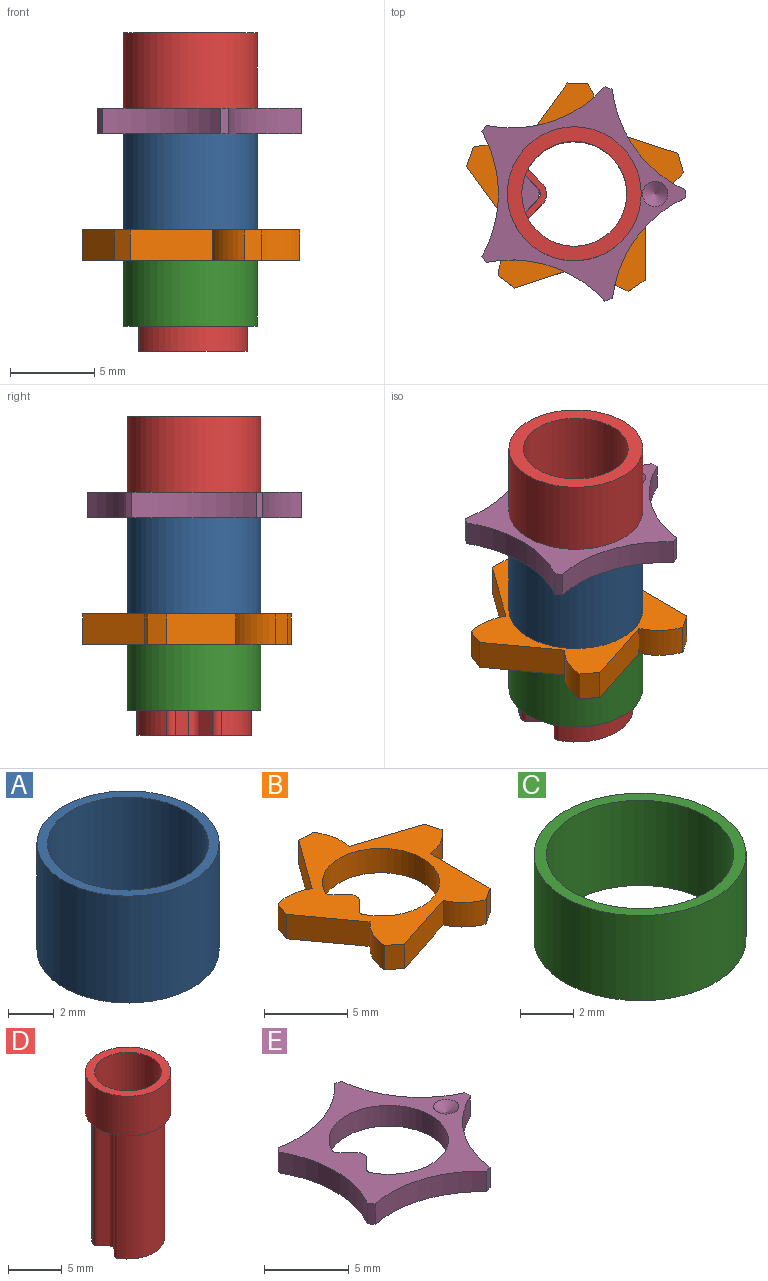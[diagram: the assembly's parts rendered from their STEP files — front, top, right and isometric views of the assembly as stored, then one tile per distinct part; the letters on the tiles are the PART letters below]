
ASSEMBLY  parts=5 mates=4
PART A: 4 faces, bbox 7.9x7.9x5.7 mm
  f0: cylinder r=3.51mm len=7.02mm, axis (0,0,-1), area 125.7mm2, adj f2,f3
  f1: cylinder r=3.97mm len=7.94mm, axis (0,0,-1), area 142.2mm2, adj f2,f3
  f2: plane 7.94x7.94mm, normal (0,0,1), area 10.8mm2, adj f0,f1
  f3: plane 7.94x7.94mm, normal (0,0,-1), area 10.8mm2, adj f0,f1
PART B: 23 faces, bbox 12.9x12.4x1.8 mm
  f0: plane 5.09x1.8mm, normal (1,0,0), area 9.2mm2, adj f1,f20,f21,f22
  f1: cylinder r=3.29mm len=2.28mm, axis (0,0,-1), area 4.8mm2, adj f0,f2,f21,f22
  f2: plane 1.8x1.15mm, normal (0.96,0.28,0), area 2.2mm2, adj f1,f3,f21,f22
  f3: plane 4.84x1.8mm, normal (0.31,0.95,0), area 9.2mm2, adj f2,f4,f21,f22
  f4: cylinder r=3.29mm len=2.56mm, axis (0,0,-1), area 4.8mm2, adj f3,f5,f21,f22
  f5: plane 1.8x1.2mm, normal (0.03,1,0), area 2.2mm2, adj f4,f6,f21,f22
  f6: plane 4.12x2.99mm, normal (-0.81,0.59,0), area 9.2mm2, adj f5,f7,f21,f22
  f7: cylinder r=3.29mm len=2.59mm, axis (0,0,-1), area 4.8mm2, adj f6,f8,f21,f22
  f8: plane 1.8x1.13mm, normal (-0.94,0.34,0), area 2.2mm2, adj f7,f9,f21,f22
  f9: plane 4.12x2.99mm, normal (-0.81,-0.59,0), area 9.2mm2, adj f8,f10,f21,f22
  f10: cylinder r=3.29mm len=2.37mm, axis (0,0,-1), area 4.8mm2, adj f9,f11,f21,f22
  f11: plane 1.8x0.95mm, normal (-0.61,-0.79,0), area 2.2mm2, adj f10,f12,f21,f22
  f12: plane 4.84x1.8mm, normal (0.31,-0.95,0), area 9.2mm2, adj f11,f13,f21,f22
  f13: cylinder r=3.29mm len=1.91mm, axis (0,0,-1), area 4.8mm2, adj f12,f20,f21,f22
  f14: cylinder r=3.53mm len=7.06mm, axis (0,0,-1), area 33.9mm2, adj f15,f19,f21,f22
  f15: cylinder r=0.3mm len=1.8mm, axis (0,0,-1), area 0.7mm2, adj f14,f16,f21,f22
  f16: plane 1.8x0.83mm, normal (0.71,-0.71,0), area 2.1mm2, adj f15,f17,f21,f22
  f17: cylinder r=0.6mm len=1.8mm, axis (0,0,-1), area 1.7mm2, adj f16,f18,f21,f22
  f18: plane 1.8x0.83mm, normal (0.71,0.71,0), area 2.1mm2, adj f17,f19,f21,f22
  f19: cylinder r=0.3mm len=1.8mm, axis (0,0,-1), area 0.7mm2, adj f14,f18,f21,f22
  f20: plane 1.8x0.99mm, normal (0.56,-0.83,0), area 2.2mm2, adj f0,f13,f21,f22
  f21: plane 12.87x12.36mm, normal (0,0,1), area 52.2mm2, adj f0,f1,f2,f3,f4,f5,f6,f7
  f22: plane 12.87x12.36mm, normal (0,0,-1), area 52.2mm2, adj f0,f1,f2,f3,f4,f5,f6,f7
PART C: 4 faces, bbox 7.9x7.9x3.9 mm
  f0: cylinder r=3.51mm len=7.02mm, axis (0,0,-1), area 86mm2, adj f2,f3
  f1: cylinder r=3.97mm len=7.94mm, axis (0,0,-1), area 97.3mm2, adj f2,f3
  f2: plane 7.94x7.94mm, normal (0,0,1), area 10.8mm2, adj f0,f1
  f3: plane 7.94x7.94mm, normal (0,0,-1), area 10.8mm2, adj f0,f1
PART D: 17 faces, bbox 7.9x7.9x18.9 mm
  f0: cylinder r=3.11mm len=18.9mm, axis (0,0,-1), area 321.8mm2, adj f2,f3,f4,f14,f15,f16
  f1: cylinder r=3.97mm len=7.94mm, axis (0,0,-1), area 112.2mm2, adj f2,f3
  f2: plane 7.94x7.94mm, normal (0,0,1), area 19.2mm2, adj f0,f1
  f3: plane 7.94x7.94mm, normal (0,0,-1), area 14mm2, adj f0,f1,f9,f10,f11
  f4: cylinder r=0.15mm len=14.4mm, axis (0,0,1), area 2.8mm2, adj f0,f5,f15,f16
  f5: plane 14.4x0.75mm, normal (0.71,0.71,0), area 15.2mm2, adj f4,f6,f15,f16
  f6: cylinder r=0.9mm len=14.4mm, axis (0,0,1), area 20.4mm2, adj f5,f7,f15,f16
  f7: plane 14.4x0.75mm, normal (0.71,-0.71,0), area 15.2mm2, adj f6,f14,f15,f16
  f8: plane 14.4x0.76mm, normal (-0.71,-0.71,0), area 15.6mm2, adj f9,f13,f15,f16
  f9: cylinder r=0.45mm len=14.4mm, axis (0,0,1), area 8.2mm2, adj f3,f8,f10,f15,f16
  f10: cylinder r=3.4mm len=14.4mm, axis (0,0,1), area 258.9mm2, adj f3,f9,f11,f15
  f11: cylinder r=0.45mm len=14.4mm, axis (0,0,1), area 8.2mm2, adj f3,f10,f12,f15,f16
  f12: plane 14.4x0.76mm, normal (-0.71,0.71,0), area 15.6mm2, adj f11,f13,f15,f16
  f13: cylinder r=0.45mm len=14.4mm, axis (0,0,1), area 10.2mm2, adj f8,f12,f15,f16
  f14: cylinder r=0.15mm len=14.4mm, axis (0,0,1), area 2.8mm2, adj f0,f7,f15,f16
  f15: plane 6.79x6.44mm, normal (0,0,-1), area 6.4mm2, adj f0,f4,f5,f6,f7,f8,f9,f10
  f16: plane 3.13x1.26mm, normal (0,0,1), area 1.3mm2, adj f0,f4,f5,f6,f7,f8,f9,f11
PART E: 19 faces, bbox 12.1x12.7x1.5 mm
  f0: cylinder r=7.5mm len=7.03mm, axis (0,0,-1), area 11.6mm2, adj f1,f15,f16,f17
  f1: cylinder r=6.6mm len=1.5mm, axis (0,0,-1), area 0.7mm2, adj f0,f2,f16,f17
  f2: cylinder r=7.5mm len=7.39mm, axis (0,0,-1), area 11.6mm2, adj f1,f3,f16,f17
  f3: cylinder r=6.6mm len=1.5mm, axis (0,0,-1), area 0.7mm2, adj f2,f4,f16,f17
  f4: cylinder r=7.5mm len=7.02mm, axis (0,0,-1), area 11.6mm2, adj f3,f5,f16,f17
  f5: cylinder r=6.6mm len=1.5mm, axis (0,0,-1), area 0.7mm2, adj f4,f6,f16,f17
  f6: cylinder r=7.5mm len=5.97mm, axis (0,0,-1), area 11.6mm2, adj f5,f7,f16,f17
  f7: cylinder r=6.6mm len=1.5mm, axis (0,0,-1), area 0.7mm2, adj f6,f8,f16,f17
  f8: cylinder r=7.5mm len=5.98mm, axis (0,0,-1), area 11.6mm2, adj f7,f15,f16,f17
  f9: cylinder r=3.53mm len=7.06mm, axis (0,0,-1), area 28.3mm2, adj f10,f14,f16,f17
  f10: cylinder r=0.3mm len=1.5mm, axis (0,0,-1), area 0.6mm2, adj f9,f11,f16,f17
  f11: plane 1.5x0.83mm, normal (0.71,-0.71,0), area 1.8mm2, adj f10,f12,f16,f17
  f12: cylinder r=0.6mm len=1.5mm, axis (0,0,-1), area 1.4mm2, adj f11,f13,f16,f17
  f13: plane 1.5x0.83mm, normal (0.71,0.71,0), area 1.8mm2, adj f12,f14,f16,f17
  f14: cylinder r=0.3mm len=1.5mm, axis (0,0,-1), area 0.6mm2, adj f9,f13,f16,f17
  f15: cylinder r=6.6mm len=1.5mm, axis (0,0,-1), area 0.7mm2, adj f0,f8,f16,f17
  f16: plane 12.69x12.07mm, normal (0,0,1), area 45.8mm2, adj f0,f1,f2,f3,f4,f5,f6,f7
  f17: plane 12.69x12.07mm, normal (0,0,-1), area 47.6mm2, adj f0,f1,f2,f3,f4,f5,f6,f7
  f18: cone r=0.75mm half-angle=60deg, axis (0,0,1), area 2mm2, adj f16
PLACE A t=(0,0,-1.2)mm
PLACE B t=(0,0,-3)mm
PLACE C t=(0,0,-6.9)mm
PLACE D t=(0,0,6)mm
PLACE E t=(0,0,4.5)mm
MATE fastened B.f14 <-> C.f0  axis (0,0,-1) through (0,0,-3)mm
MATE fastened E.f1 <-> D.f0  axis (0,0,-1) through (0,0,6)mm
MATE fastened A.f0 <-> E.f1  axis (0,0,-1) through (0,0,4.5)mm
MATE fastened A.f0 <-> B.f14  axis (0,0,-1) through (0,0,-1.2)mm
